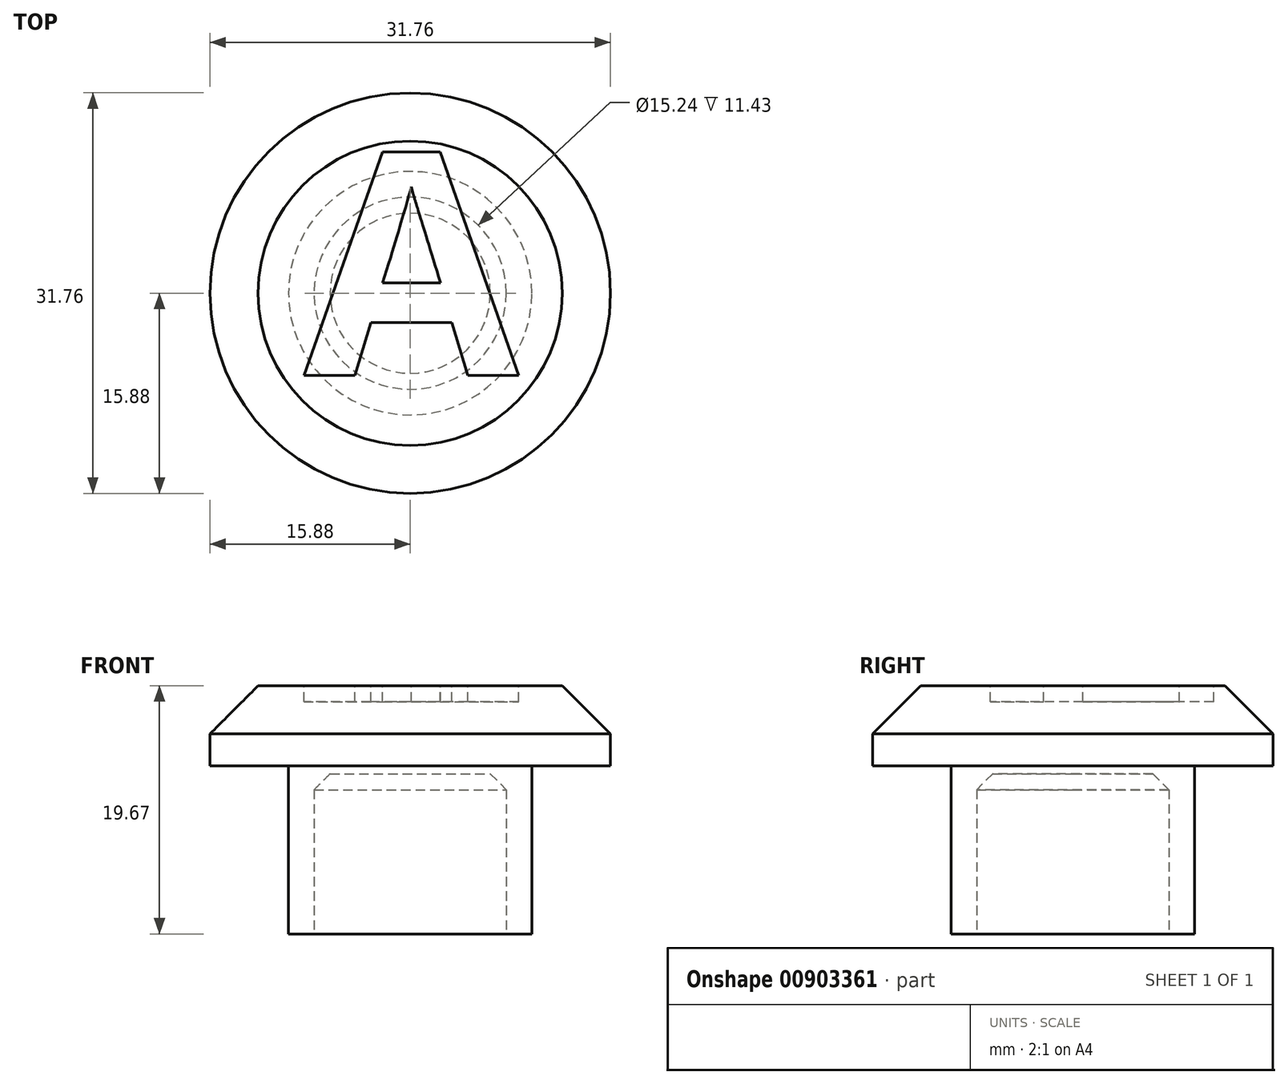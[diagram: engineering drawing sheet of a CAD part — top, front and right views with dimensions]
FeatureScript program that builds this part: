
annotation { "Feature Type Name" : "Feature", "Feature Type Description" : "" }
export const myFeature = defineFeature(function(context is Context, id is Id, definition is map)
    precondition{}
    {
        {
            var Q0;
            Q0=qCreatedBy(makeId("Front.planeOp"),FACE);
            var sketch = newSketch(context, id + "F0", { "sketchPlane" : qUnion([Q0])});
            skLineSegment(sketch, "E0", {"start": v(0, 0) * mm, "end": v(9.65, 0) * mm});
            skLineSegment(sketch, "E1", {"start": v(9.65, 0) * mm, "end": v(9.65, 13.32) * mm});
            skLineSegment(sketch, "E2", {"start": v(9.65, 13.32) * mm, "end": v(15.88, 13.32) * mm});
            skLineSegment(sketch, "E3", {"start": v(15.88, 13.32) * mm, "end": v(15.88, 19.67) * mm});
            skLineSegment(sketch, "E4", {"start": v(15.88, 19.67) * mm, "end": v(0, 19.67) * mm});
            skLineSegment(sketch, "E5", {"start": v(0, 19.67) * mm, "end": v(0, 0) * mm});
            skLineSegment(sketch, "E6", {"start": v(0, 35.05) * mm, "end": v(0, -20.6) * mm, "construction": true});
            skSolve(sketch);
        }
        {
            var Q0;
            Q0=makeQuery(id+"F0.imprint","IMPRINT",FACE,{"disambiguationData":[TD([[makeQuery(id+"F0.imprint","IMPRINT",EDGE,{"derivedFrom":sQuery(id+"F0.wireOp",EDGE,"E0")}),1.0]])]});
            var Q1;
            Q1=sQuery(id+"F0.wireOp",EDGE,"E6");
            revolve(context, id + "F1", {"surfaceOperationType" : NewSurfaceOperationType.NEW, "entities" : qUnion([Q0]), "axis" : qUnion([Q1]), "revolveType" : RevolveType.FULL});
        }
        {
            var Q0;
            Q0=makeQuery(id+"F1.opRevolve","SWEPT_FACE",FACE,{"disambiguationData":[OSD([sQuery(id+"F0.wireOp",EDGE,"E4")])]});
            var sketch = newSketch(context, id + "F2", { "sketchPlane" : qUnion([Q0])});
            skText(sketch, "E7", { "text": "A", "fontName": "OpenSans-Bold.ttf"});
            const initialGuessF2  = {"E7": [-0.00843, -0.00652, 1, 0, 0.01778]};
            skSetInitialGuess(sketch, initialGuessF2);
            skSolve(sketch);
        }
        {
            var Q0;
            Q0=makeQuery(id+"F1.opRevolve","SWEPT_EDGE",EDGE,{"disambiguationData":[OSD([sQuery(id+"F0.wireOp",EDGE,"E3"),sQuery(id+"F0.wireOp",EDGE,"E4")])]});
            chamfer(context, id + "F3", {"entities" : qUnion([Q0]), "width" : 3.8 * mm, "tangentPropagation" : true});
        }
        {
            var Q0;
            Q0=makeQuery(id+"F1.opRevolve","SWEPT_FACE",FACE,{"disambiguationData":[OSD([sQuery(id+"F0.wireOp",EDGE,"E0")])]});
            var sketch = newSketch(context, id + "F4", { "sketchPlane" : qUnion([Q0])});
            skCircle(sketch, "E8", {"center": v(0, 0) * mm, "radius": 7.62 * mm});
            skSolve(sketch);
        }
        {
            var Q0;
            {var subQ8=sQuery(id+"F4.wireOp",EDGE,"ygCifC7E-R5CW-Vsgm-YzDT-VXsedIujfA2w");Q0=makeQuery(id+"F4.imprint","IMPRINT",FACE,{"disambiguationData":[TD([[makeQuery(id+"F4.imprint","IMPRINT",EDGE,{"derivedFrom":subQ8}),1.0]])]});}
            var Q1;
            Q1 = qSketchRegion(id + "F2", true);
            var Q2;
            Q2=makeQuery(id+"F1.opRevolve","SWEPT_FACE",FACE,{"disambiguationData":[OSD([sQuery(id+"F0.wireOp",EDGE,"E2")])]});
            extrude(context, id + "F5", {"entities" : qUnion([Q0, Q1]), "operationType" : NewBodyOperationType.REMOVE, "oppositeDirection" : true, "depth" : 1.27 * mm, "endBoundEntityFace" : qUnion([Q2]), "offsetDistance" : 25.4 * mm});
        }
        {
            var Q0;
            Q0=makeQuery(id+"F2.imprint","IMPRINT",FACE,{"disambiguationData":[TD([[makeQuery(id+"F2.imprint","IMPRINT",EDGE,{"derivedFrom":sQuery(id+"F2.wireOp",EDGE,"E7.sketch_text.stroke-0")}),-1.0]])]});
            var Q1;
            Q1 = qSketchRegion(id + "F4", true);
            extrude(context, id + "F6", {"entities" : qUnion([Q0, Q1]), "operationType" : NewBodyOperationType.REMOVE, "depth" : 12.7 * mm, "offsetDistance" : 25.4 * mm});
        }
        {
            var Q0;
            Q0=makeQuery(id+"F6.boolean.opBoolean","COPY",FACE,{"derivedFrom":makeQuery(id+"F6.opExtrude","CAP_FACE",FACE,{"disambiguationData":[OSD([sQuery(id+"F4.wireOp",EDGE,"E8")])],"isStart":false})});
            chamfer(context, id + "F7", {"entities" : qUnion([Q0]), "width" : 1.27 * mm, "tangentPropagation" : true});
        }
    });
